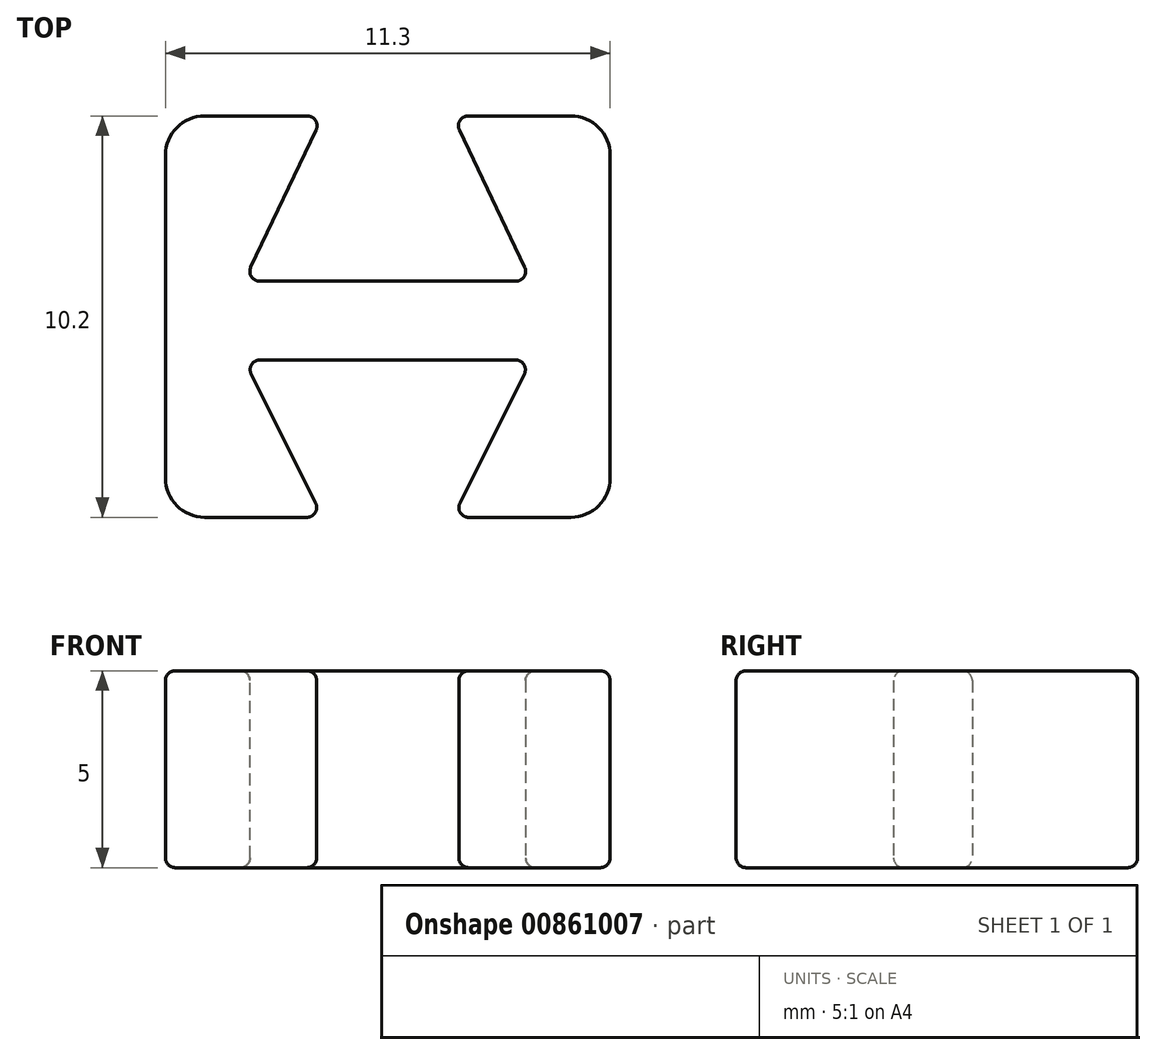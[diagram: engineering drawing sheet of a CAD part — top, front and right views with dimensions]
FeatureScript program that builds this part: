
annotation { "Feature Type Name" : "Feature", "Feature Type Description" : "" }
export const myFeature = defineFeature(function(context is Context, id is Id, definition is map)
    precondition{}
    {
        {
            var Q0;
            Q0=qCreatedBy(makeId("Top.planeOp"),FACE);
            var sketch = newSketch(context, id + "F0", { "sketchPlane" : qUnion([Q0])});
            skLineSegment(sketch, "E0", {"start": v(-1.65, 5.9) * mm, "end": v(-1.65, -13.03) * mm, "construction": true});
            skLineSegment(sketch, "E1", {"start": v(1.65, 6.14) * mm, "end": v(1.65, -12.87) * mm, "construction": true});
            skLineSegment(sketch, "E2", {"start": v(-3.65, 6.14) * mm, "end": v(-3.65, -12.95) * mm, "construction": true});
            skLineSegment(sketch, "E3", {"start": v(3.65, 6.86) * mm, "end": v(3.65, -12.6) * mm, "construction": true});
            skLineSegment(sketch, "E4", {"start": v(-3.65, 0) * mm, "end": v(3.65, 0) * mm});
            skLineSegment(sketch, "E5", {"start": v(-5.78, 4.2) * mm, "end": v(-1.65, 4.2) * mm});
            skLineSegment(sketch, "E6", {"start": v(-1.65, 4.2) * mm, "end": v(-3.65, 0) * mm});
            skLineSegment(sketch, "E7", {"start": v(1.65, 4.2) * mm, "end": v(3.65, 0) * mm});
            skLineSegment(sketch, "E8", {"start": v(-5.65, 4.2) * mm, "end": v(-5.65, -6) * mm});
            skLineSegment(sketch, "E9", {"start": v(5.65, 4.2) * mm, "end": v(5.65, -6) * mm});
            skLineSegment(sketch, "E10.trimOffspring", {"start": v(1.65, 4.2) * mm, "end": v(5.65, 4.2) * mm});
            skPoint(sketch, "E11.orphan", {"position": v(-5.62, 0) * mm});
            skLineSegment(sketch, "E12.trimOffspring", {"start": v(5.65, 0) * mm, "end": v(5.73, 0) * mm});
            skLineSegment(sketch, "E13", {"start": v(-5.65, -6) * mm, "end": v(-1.65, -6) * mm});
            skLineSegment(sketch, "E14", {"start": v(-1.65, -6) * mm, "end": v(-3.65, -2) * mm});
            skLineSegment(sketch, "E15", {"start": v(1.65, -6) * mm, "end": v(3.65, -2) * mm});
            skLineSegment(sketch, "E16.trimOffspring", {"start": v(1.65, -6) * mm, "end": v(5.65, -6) * mm});
            skLineSegment(sketch, "E17.trimOffspring", {"start": v(-3.65, -2) * mm, "end": v(3.65, -2) * mm});
            skPoint(sketch, "E18.orphan", {"position": v(-7.18, -6) * mm});
            skPoint(sketch, "E19.start.orphan", {"position": v(-7.14, -2) * mm});
            skPoint(sketch, "E20.orphan", {"position": v(-5.65, 5.58) * mm});
            skSolve(sketch);
        }
        {
            var Q0;
            Q0=makeQuery(id+"F0.imprint","IMPRINT",FACE,{"disambiguationData":[TD([[makeQuery(id+"F0.imprint","IMPRINT",EDGE,{"derivedFrom":sQuery(id+"F0.wireOp",EDGE,"E4")}),-1.0]])]});
            extrude(context, id + "F1", {"entities" : qUnion([Q0]), "depth" : 5 * mm, "offsetDistance" : 25.4 * mm});
        }
        {
            var Q0;
            Q0=makeQuery(id+"F1.opExtrude","SWEPT_EDGE",EDGE,{"disambiguationData":[OSD([sQuery(id+"F0.wireOp",EDGE,"E8"),sQuery(id+"F0.wireOp",EDGE,"E13")])]});
            var Q1;
            Q1=makeQuery(id+"F1.opExtrude","SWEPT_EDGE",EDGE,{"disambiguationData":[OSD([sQuery(id+"F0.wireOp",EDGE,"E5"),sQuery(id+"F0.wireOp",EDGE,"E8")])]});
            var Q2;
            Q2=makeQuery(id+"F1.opExtrude","SWEPT_EDGE",EDGE,{"disambiguationData":[OSD([sQuery(id+"F0.wireOp",EDGE,"E9"),sQuery(id+"F0.wireOp",EDGE,"E16.trimOffspring")])]});
            var Q3;
            Q3=makeQuery(id+"F1.opExtrude","SWEPT_EDGE",EDGE,{"disambiguationData":[OSD([sQuery(id+"F0.wireOp",EDGE,"E9"),sQuery(id+"F0.wireOp",EDGE,"E10.trimOffspring")])]});
            fillet(context, id + "F2", {"entities" : qUnion([Q0, Q1, Q2, Q3]), "radius" : 1 * mm, "tangentPropagation" : true, "allowEdgeOverflow" : false});
        }
        {
            var Q0;
            Q0=makeQuery(id+"F1.opExtrude","SWEPT_EDGE",EDGE,{"disambiguationData":[OSD([sQuery(id+"F0.wireOp",EDGE,"E7"),sQuery(id+"F0.wireOp",EDGE,"E10.trimOffspring")])]});
            var Q1;
            Q1=makeQuery(id+"F1.opExtrude","SWEPT_EDGE",EDGE,{"disambiguationData":[OSD([sQuery(id+"F0.wireOp",EDGE,"E5"),sQuery(id+"F0.wireOp",EDGE,"E6")])]});
            var Q2;
            Q2=makeQuery(id+"F1.opExtrude","SWEPT_EDGE",EDGE,{"disambiguationData":[OSD([sQuery(id+"F0.wireOp",EDGE,"E4"),sQuery(id+"F0.wireOp",EDGE,"E7")])]});
            var Q3;
            Q3=makeQuery(id+"F1.opExtrude","SWEPT_EDGE",EDGE,{"disambiguationData":[OSD([sQuery(id+"F0.wireOp",EDGE,"E4"),sQuery(id+"F0.wireOp",EDGE,"E6")])]});
            var Q4;
            Q4=makeQuery(id+"F1.opExtrude","SWEPT_EDGE",EDGE,{"disambiguationData":[OSD([sQuery(id+"F0.wireOp",EDGE,"E14"),sQuery(id+"F0.wireOp",EDGE,"E17.trimOffspring")])]});
            var Q5;
            Q5=makeQuery(id+"F1.opExtrude","SWEPT_EDGE",EDGE,{"disambiguationData":[OSD([sQuery(id+"F0.wireOp",EDGE,"E15"),sQuery(id+"F0.wireOp",EDGE,"E17.trimOffspring")])]});
            var Q6;
            Q6=makeQuery(id+"F1.opExtrude","SWEPT_EDGE",EDGE,{"disambiguationData":[OSD([sQuery(id+"F0.wireOp",EDGE,"E15"),sQuery(id+"F0.wireOp",EDGE,"E16.trimOffspring")])]});
            var Q7;
            Q7=makeQuery(id+"F1.opExtrude","SWEPT_EDGE",EDGE,{"disambiguationData":[OSD([sQuery(id+"F0.wireOp",EDGE,"E13"),sQuery(id+"F0.wireOp",EDGE,"E14")])]});
            fillet(context, id + "F3", {"entities" : qUnion([Q0, Q1, Q2, Q3, Q4, Q5, Q6, Q7]), "radius" : 0.25 * mm, "tangentPropagation" : true, "allowEdgeOverflow" : false});
        }
        {
            var Q0;
            {var subQ0=sQuery(id+"F0.wireOp",EDGE,"E8");var subQ1=sQuery(id+"F0.wireOp",EDGE,"E5");Q0=makeQuery(id+"F2.opFillet","BLEND_EDGE",EDGE,{"blendedFrom":[makeQuery(id+"F1.opExtrude","SWEPT_EDGE",EDGE,{"disambiguationData":[OSD([subQ1,subQ0])]}),makeQuery(id+"F1.opExtrude","CAP_FACE",FACE,{"disambiguationData":[OSD([sQuery(id+"F0.wireOp",EDGE,"E4"),subQ1,sQuery(id+"F0.wireOp",EDGE,"E6"),sQuery(id+"F0.wireOp",EDGE,"E7"),subQ0,sQuery(id+"F0.wireOp",EDGE,"E9"),sQuery(id+"F0.wireOp",EDGE,"E10.trimOffspring"),sQuery(id+"F0.wireOp",EDGE,"E13"),sQuery(id+"F0.wireOp",EDGE,"E14"),sQuery(id+"F0.wireOp",EDGE,"E15"),sQuery(id+"F0.wireOp",EDGE,"E16.trimOffspring"),sQuery(id+"F0.wireOp",EDGE,"E17.trimOffspring")])],"isStart":false})],"blendedInto":[makeQuery(id+"F1.opExtrude","CAP_FACE",FACE,{"disambiguationData":[OSD([sQuery(id+"F0.wireOp",EDGE,"E4"),subQ1,sQuery(id+"F0.wireOp",EDGE,"E6"),sQuery(id+"F0.wireOp",EDGE,"E7"),subQ0,sQuery(id+"F0.wireOp",EDGE,"E9"),sQuery(id+"F0.wireOp",EDGE,"E10.trimOffspring"),sQuery(id+"F0.wireOp",EDGE,"E13"),sQuery(id+"F0.wireOp",EDGE,"E14"),sQuery(id+"F0.wireOp",EDGE,"E15"),sQuery(id+"F0.wireOp",EDGE,"E16.trimOffspring"),sQuery(id+"F0.wireOp",EDGE,"E17.trimOffspring")])],"isStart":false})]});}
            var Q1;
            Q1=makeQuery(id+"F1.opExtrude","CAP_EDGE",EDGE,{"disambiguationData":[OSD([sQuery(id+"F0.wireOp",EDGE,"E10.trimOffspring")])],"isStart":true});
            fillet(context, id + "F4", {"entities" : qUnion([Q0, Q1]), "radius" : 0.25 * mm, "tangentPropagation" : true, "allowEdgeOverflow" : false});
        }
    });
